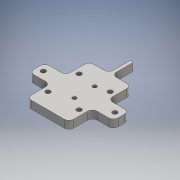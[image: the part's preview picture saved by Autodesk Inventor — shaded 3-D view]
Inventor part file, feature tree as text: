
AUTODESK INVENTOR PART (.ipt)
format: ipt  version: 2016 SP1 (Build 200210100, 210)  size: 509,440 bytes
history: native  units: mm
features: extrude x14, sketch x12, projected_geometry x6, fillet x5, hole x1
ambient origin geometry x8: Origin, YZ Plane, XZ Plane, XY Plane, X Axis, Y Axis, Z Axis, Center Point
bodies: Solid1 (feature_tree)
feature tree (38):
  extrude  "Extrusion1"  Depth=3.0mm
  extrude  "Extrusion2"  Depth=10.0mm
  extrude  "Extrusion3"  Depth=3.0mm
  extrude  "Extrusion4"  Depth=20.0mm
  extrude  "Extrusion5"  Depth=10.0mm
  hole  "Hole1"  [1 undecoded]
  fillet  "Fillet5"  Radius=40.0mm
  fillet  "Fillet7"  Radius=10.0mm
  extrude  "Extrusion7"  Depth=10.0mm
  fillet  "Fillet9"  Radius=10.0mm
  extrude  "Extrusion8"  Depth=2.5mm
  extrude  "Extrusion10"  Depth=2.0mm
  fillet  "Fillet10"  Radius=2.0mm
  fillet  "Fillet11"  Radius=12.0mm
  extrude  "Extrusion11"  Depth=2.0mm
  extrude  "Extrusion12"  Depth=6.5mm
  extrude  "Extrusion13"  Depth=10.0mm TaperAngle=0.0deg
  extrude  "Extrusion14"  Depth=10.0mm
  extrude  "Extrusion9"  Depth=40.0mm
  extrude  "Extrusion6"  Depth=15.0mm
  sketch  "Sketch3"  dims[d0=3.0mm d1=3.0mm]
  sketch  "Sketch4"  dims[d2=20.0mm d3=10.0mm]
  sketch  "Sketch5"  dims[d4=3.0mm d5=3.0mm]
  sketch  "Sketch9"  dims[d6=20.0mm d7=20.0mm]
  sketch  "Sketch11"  dims[d8=20.0mm d9=10.0mm]
  sketch  "Sketch12"  dims[d10=30.0mm d11=15.0mm d12=40.0mm d13=10.0mm]
  projected_geometry  "Projected Loop2"
  sketch  "Sketch13"  dims[d14=5.0mm d15=0.0mm d16=4.0mm d20=10.0mm d21=0.0mm]
  projected_geometry  "Projected Loop3"
  sketch  "Sketch14"  dims[d23=2.5mm d24=2.5mm]
  sketch  "Sketch15"  dims[d25=15.0mm d26=2.0mm d27=2.0mm d28=12.0mm]
  sketch  "Sketch16"  dims[d29=2.5mm d30=6.0mm d31=4.0mm d32=2.0mm d33=90.0deg d34=8.0mm d35=20.594885mm d36=6.3mm]
  projected_geometry  "Projected Loop5"
  projected_geometry  "Projected Loop6"
  sketch  "Sketch17"  dims[d37=6.5mm d38=6.5mm]
  projected_geometry  "Projected Loop7"
  sketch  "Sketch18"  dims[d39=8.0mm d40=0.0mm d47=8.0mm d48=0.0mm d77=10.0mm d78=40.0mm d79=15.0mm d80=3.0mm d81=3.0mm d82=46.0mm d83=54.0mm d84=23.0mm d85=27.0mm d86=8.0mm d87=0.0mm d90=8.0mm d91=0.0mm d94=1.0mm d96=0.0mm d97=0.0mm d110=2.0mm d111=0.7mm d112=4.0mm d115=4.0mm d116=1.3mm d117=6.0mm d118=2.5mm d119=2.0mm d121=27.0mm d122=13.5mm d123=10.0mm d124=0.0mm d125=3.0mm d126=3.0mm d128=6.0mm d129=3.0mm d130=10.0mm d131=0.0mm d132=3.0mm d133=21.0mm d134=4.0mm d136=11.0mm d137=10.0mm d138=0.0mm d139=0.0mm d140=0.0mm d141=22.0mm d142=14.0mm d143=1.0mm d144=1.0mm d145=10.0mm d146=0.0mm d147=3.0mm d148=1.0mm d149=8.0mm d150=10.0mm d151=0.0mm d152=0.0mm d153=10.0mm d154=0.0mm d155=10.0mm d156=0.0mm d157=10.0mm d158=0.0mm]
  projected_geometry  "Projected Loop8"
note: 1 required parameter value undecoded (feature->parameter linkage not recoverable at this tier; creation-order binding heuristic only, values carry confidence <= 0.55)
